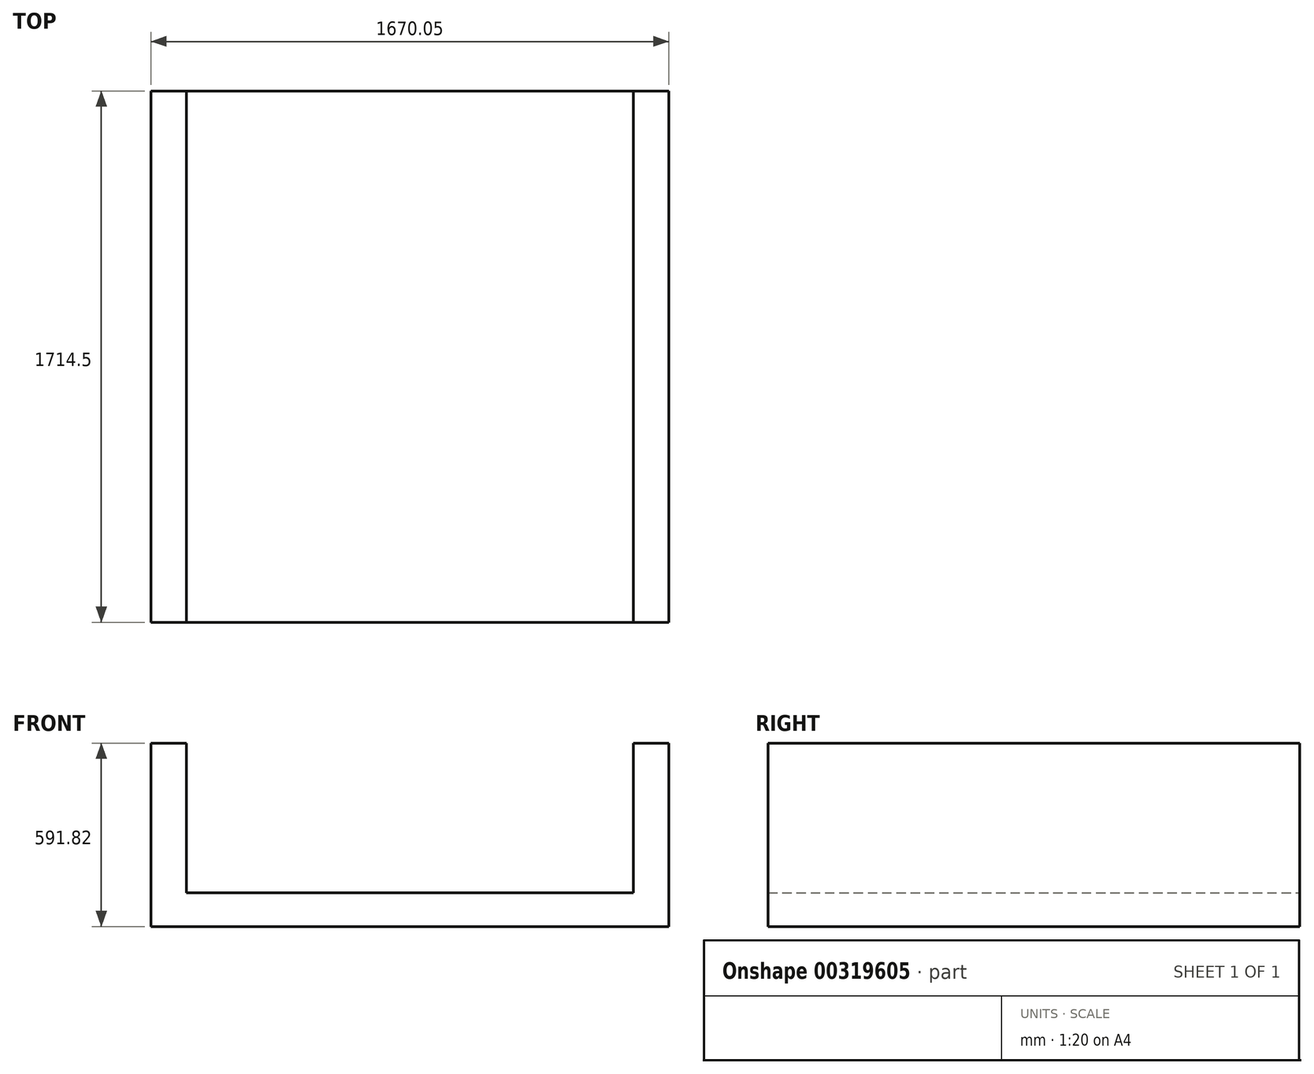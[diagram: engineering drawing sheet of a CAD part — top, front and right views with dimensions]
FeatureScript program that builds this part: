
annotation { "Feature Type Name" : "Feature", "Feature Type Description" : "" }
export const myFeature = defineFeature(function(context is Context, id is Id, definition is map)
    precondition{}
    {
        {
            var Q0;
            Q0=qCreatedBy(makeId("Front.planeOp"),FACE);
            var sketch = newSketch(context, id + "F0", { "sketchPlane" : qUnion([Q0])});
            skLineSegment(sketch, "E0", {"start": v(0, 0) * mm, "end": v(1670.05, 0) * mm});
            skLineSegment(sketch, "E1", {"start": v(1670.05, 0) * mm, "end": v(1670.05, 591.82) * mm});
            skLineSegment(sketch, "E2", {"start": v(1670.05, 591.82) * mm, "end": v(1555.75, 591.82) * mm});
            skLineSegment(sketch, "E3", {"start": v(1555.75, 591.82) * mm, "end": v(1555.75, 109.22) * mm});
            skLineSegment(sketch, "E4", {"start": v(1555.75, 109.22) * mm, "end": v(114.3, 109.22) * mm});
            skLineSegment(sketch, "E5", {"start": v(114.3, 109.22) * mm, "end": v(114.3, 591.82) * mm});
            skLineSegment(sketch, "E6", {"start": v(114.3, 591.82) * mm, "end": v(0, 591.82) * mm});
            skLineSegment(sketch, "E7", {"start": v(0, 591.82) * mm, "end": v(0, 0) * mm});
            skSolve(sketch);
        }
        {
            var Q0;
            Q0=makeQuery(id+"F0.imprint","IMPRINT",FACE,{"disambiguationData":[TD([[makeQuery(id+"F0.imprint","IMPRINT",EDGE,{"derivedFrom":sQuery(id+"F0.wireOp",EDGE,"E0")}),1.0]])]});
            extrude(context, id + "F1", {"entities" : qUnion([Q0]), "depth" : 1714.5 * mm});
        }
    });
